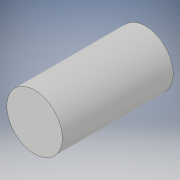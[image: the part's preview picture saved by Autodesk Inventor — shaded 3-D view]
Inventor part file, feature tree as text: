
AUTODESK INVENTOR PART (.ipt)
format: ipt  version: 2017 (Build 210142000, 142)  size: 88,576 bytes
history: native  units: in
note: dims shown in document units (in); Inventor stores cm internally (conversion verified against a paired STEP export)
features: extrude x1, sketch x1
ambient origin geometry x8: Origin, YZ Plane, XZ Plane, XY Plane, X Axis, Y Axis, Z Axis, Center Point
bodies: Solid1 (feature_tree)
feature tree (2):
  extrude  "Extrusion1"  Depth=0.5in TaperAngle=0.0deg
  sketch  "Sketch1"  dims[d0=0.25in d1=0.5in d2=0.0in]
